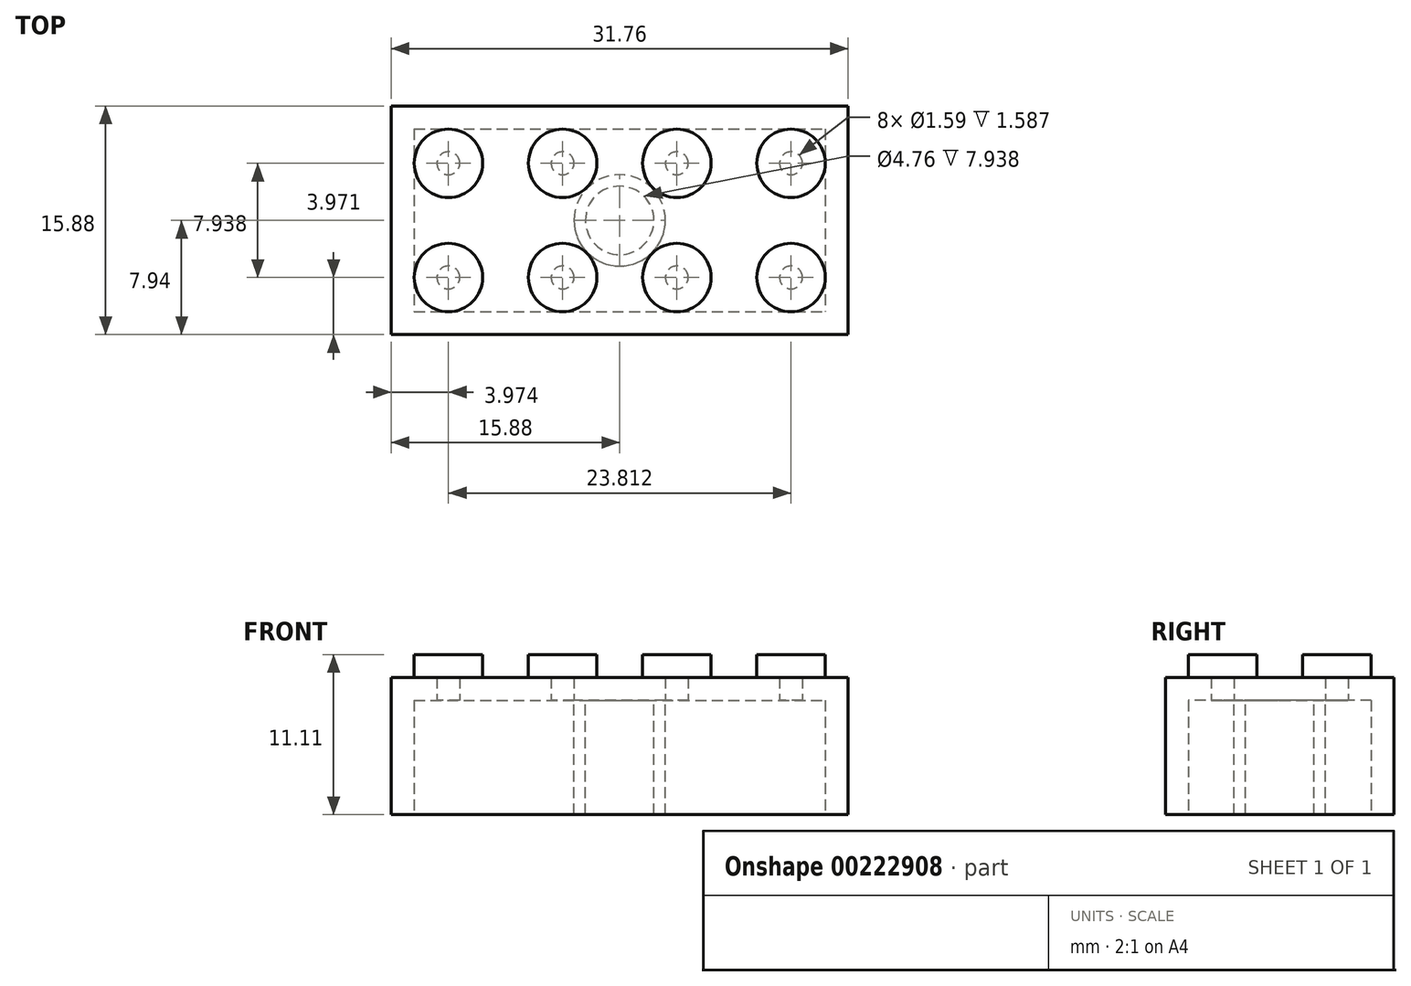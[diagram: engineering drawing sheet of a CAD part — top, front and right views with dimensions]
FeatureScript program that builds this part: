
annotation { "Feature Type Name" : "Feature", "Feature Type Description" : "" }
export const myFeature = defineFeature(function(context is Context, id is Id, definition is map)
    precondition{}
    {
        {
            var Q0;
            Q0=qCreatedBy(makeId("Top.planeOp"),FACE);
            var sketch = newSketch(context, id + "F0", { "sketchPlane" : qUnion([Q0])});
            skLineSegment(sketch, "E0.bottom", {"start": v(-15.88, 7.94) * mm, "end": v(15.88, 7.94) * mm});
            skLineSegment(sketch, "E0.top", {"start": v(-15.88, -7.94) * mm, "end": v(15.88, -7.94) * mm});
            skLineSegment(sketch, "E0.left", {"start": v(-15.88, 7.94) * mm, "end": v(-15.88, -7.94) * mm});
            skLineSegment(sketch, "E0.right", {"start": v(15.88, 7.94) * mm, "end": v(15.88, -7.94) * mm});
            skPoint(sketch, "E0.middle", {"position": v(0, 0) * mm});
            skCircle(sketch, "E1", {"center": v(-11.9, 3.97) * mm, "radius": 2.38 * mm});
            skCircle(sketch, "E2.0.1.0", {"center": v(-11.9, -3.97) * mm, "radius": 2.38 * mm});
            skCircle(sketch, "E2.1.0.0", {"center": v(-3.97, 3.97) * mm, "radius": 2.38 * mm});
            skCircle(sketch, "E2.1.1.0", {"center": v(-3.97, -3.97) * mm, "radius": 2.38 * mm});
            skLineSegment(sketch, "E2.direction1", {"start": v(-11.9, 3.97) * mm, "end": v(-3.97, 3.97) * mm, "construction": true});
            skLineSegment(sketch, "E2.direction2", {"start": v(-11.9, 3.97) * mm, "end": v(-11.9, -3.97) * mm, "construction": true});
            skCircle(sketch, "E3.0.2.0", {"center": v(3.97, 3.97) * mm, "radius": 2.38 * mm});
            skCircle(sketch, "E3.0.2.1", {"center": v(3.97, -3.97) * mm, "radius": 2.38 * mm});
            skCircle(sketch, "E3.0.3.0", {"center": v(11.9, 3.97) * mm, "radius": 2.38 * mm});
            skCircle(sketch, "E3.0.3.1", {"center": v(11.9, -3.97) * mm, "radius": 2.38 * mm});
            skSolve(sketch);
        }
        {
            var Q0;
            Q0=makeQuery(id+"F0.imprint","IMPRINT",FACE,{"disambiguationData":[TD([[makeQuery(id+"F0.imprint","IMPRINT",EDGE,{"derivedFrom":sQuery(id+"F0.wireOp",EDGE,"E0.bottom")}),-1.0]])]});
            extrude(context, id + "F1", {"entities" : qUnion([Q0]), "depth" : 3.17 * mm});
        }
        {
            var Q0;
            Q0=makeQuery(id+"F0.imprint","IMPRINT",FACE,{"disambiguationData":[TD([[makeQuery(id+"F0.imprint","IMPRINT",EDGE,{"derivedFrom":sQuery(id+"F0.wireOp",EDGE,"E1")}),1.0]])]});
            var Q1;
            Q1=makeQuery(id+"F0.imprint","IMPRINT",FACE,{"disambiguationData":[TD([[makeQuery(id+"F0.imprint","IMPRINT",EDGE,{"derivedFrom":sQuery(id+"F0.wireOp",EDGE,"E2.1.0.0")}),1.0]])]});
            var Q2;
            Q2=makeQuery(id+"F0.imprint","IMPRINT",FACE,{"disambiguationData":[TD([[makeQuery(id+"F0.imprint","IMPRINT",EDGE,{"derivedFrom":sQuery(id+"F0.wireOp",EDGE,"E2.1.1.0")}),1.0]])]});
            var Q3;
            Q3=makeQuery(id+"F0.imprint","IMPRINT",FACE,{"disambiguationData":[TD([[makeQuery(id+"F0.imprint","IMPRINT",EDGE,{"derivedFrom":sQuery(id+"F0.wireOp",EDGE,"E2.0.1.0")}),1.0]])]});
            var Q4;
            Q4=makeQuery(id+"F0.imprint","IMPRINT",FACE,{"disambiguationData":[TD([[makeQuery(id+"F0.imprint","IMPRINT",EDGE,{"derivedFrom":sQuery(id+"F0.wireOp",EDGE,"E3.0.2.0")}),1.0]])]});
            var Q5;
            Q5=makeQuery(id+"F0.imprint","IMPRINT",FACE,{"disambiguationData":[TD([[makeQuery(id+"F0.imprint","IMPRINT",EDGE,{"derivedFrom":sQuery(id+"F0.wireOp",EDGE,"E3.0.3.0")}),1.0]])]});
            var Q6;
            Q6=makeQuery(id+"F0.imprint","IMPRINT",FACE,{"disambiguationData":[TD([[makeQuery(id+"F0.imprint","IMPRINT",EDGE,{"derivedFrom":sQuery(id+"F0.wireOp",EDGE,"E3.0.3.1")}),1.0]])]});
            var Q7;
            Q7=makeQuery(id+"F0.imprint","IMPRINT",FACE,{"disambiguationData":[TD([[makeQuery(id+"F0.imprint","IMPRINT",EDGE,{"derivedFrom":sQuery(id+"F0.wireOp",EDGE,"E3.0.2.1")}),1.0]])]});
            extrude(context, id + "F2", {"entities" : qUnion([Q0, Q1, Q2, Q3, Q4, Q5, Q6, Q7]), "operationType" : NewBodyOperationType.ADD, "depth" : 4.76 * mm});
        }
        {
            var Q0;
            {var subQ0=sQuery(id+"F0.wireOp",EDGE,"E2.1.1.0");var subQ1=sQuery(id+"F0.wireOp",EDGE,"E2.1.0.0");var subQ2=sQuery(id+"F0.wireOp",EDGE,"E2.0.1.0");var subQ3=sQuery(id+"F0.wireOp",EDGE,"E1");Q0=makeQuery(id+"F2.boolean.opBoolean","MERGE",FACE,{"derivedFrom":[makeQuery(id+"F1.opExtrude","CAP_FACE",FACE,{"disambiguationData":[OSD([sQuery(id+"F0.wireOp",EDGE,"E0.bottom"),sQuery(id+"F0.wireOp",EDGE,"E0.top"),sQuery(id+"F0.wireOp",EDGE,"E0.left"),sQuery(id+"F0.wireOp",EDGE,"E0.right"),subQ3,subQ2,subQ1,subQ0])],"isStart":true}),makeQuery(id+"F2.opExtrude","CAP_FACE",FACE,{"disambiguationData":[OSD([subQ3])],"isStart":true}),makeQuery(id+"F2.opExtrude","CAP_FACE",FACE,{"disambiguationData":[OSD([subQ2])],"isStart":true}),makeQuery(id+"F2.opExtrude","CAP_FACE",FACE,{"disambiguationData":[OSD([subQ1])],"isStart":true}),makeQuery(id+"F2.opExtrude","CAP_FACE",FACE,{"disambiguationData":[OSD([subQ0])],"isStart":true})]});}
            shell(context, id + "F3", {"entities" : qUnion([Q0]), "thickness" : 1.59 * mm});
        }
        {
            var Q0;
            Q0=makeQuery(id+"F3.opShell","OFFSET_FACE",FACE,{"disambiguationData":[OSD([sQuery(id+"F0.wireOp",EDGE,"E0.bottom"),sQuery(id+"F0.wireOp",EDGE,"E0.top"),sQuery(id+"F0.wireOp",EDGE,"E0.left"),sQuery(id+"F0.wireOp",EDGE,"E0.right"),sQuery(id+"F0.wireOp",EDGE,"E1"),sQuery(id+"F0.wireOp",EDGE,"E2.0.1.0"),sQuery(id+"F0.wireOp",EDGE,"E2.1.0.0"),sQuery(id+"F0.wireOp",EDGE,"E2.1.1.0")])]});
            var sketch = newSketch(context, id + "F4", { "sketchPlane" : qUnion([Q0])});
            skCircle(sketch, "E4", {"center": v(0, 0) * mm, "radius": 3.18 * mm});
            skCircle(sketch, "E5", {"center": v(0, 0) * mm, "radius": 2.38 * mm});
            skSolve(sketch);
        }
        {
            var Q0;
            Q0=makeQuery(id+"F4.imprint","IMPRINT",FACE,{"disambiguationData":[TD([[makeQuery(id+"F4.imprint","IMPRINT",EDGE,{"derivedFrom":sQuery(id+"F4.wireOp",EDGE,"E4")}),1.0]])]});
            extrude(context, id + "F5", {"entities" : qUnion([Q0]), "operationType" : NewBodyOperationType.ADD, "depth" : 1.59 * mm});
        }
        {
            var Q0;
            {var subQ0=sQuery(id+"F0.wireOp",EDGE,"E3.0.3.1");var subQ1=sQuery(id+"F0.wireOp",EDGE,"E3.0.3.0");var subQ2=sQuery(id+"F0.wireOp",EDGE,"E3.0.2.1");var subQ3=sQuery(id+"F0.wireOp",EDGE,"E3.0.2.0");var subQ4=sQuery(id+"F0.wireOp",EDGE,"E2.1.1.0");var subQ5=sQuery(id+"F0.wireOp",EDGE,"E2.1.0.0");var subQ6=sQuery(id+"F0.wireOp",EDGE,"E2.0.1.0");var subQ7=sQuery(id+"F0.wireOp",EDGE,"E1");Q0=makeQuery(id+"F2.boolean.opBoolean","MERGE",FACE,{"derivedFrom":[makeQuery(id+"F1.opExtrude","CAP_FACE",FACE,{"disambiguationData":[OSD([sQuery(id+"F0.wireOp",EDGE,"E0.bottom"),sQuery(id+"F0.wireOp",EDGE,"E0.top"),sQuery(id+"F0.wireOp",EDGE,"E0.left"),sQuery(id+"F0.wireOp",EDGE,"E0.right"),subQ7,subQ6,subQ5,subQ4,subQ3,subQ2,subQ1,subQ0])],"isStart":true}),makeQuery(id+"F2.opExtrude","CAP_FACE",FACE,{"disambiguationData":[OSD([subQ7])],"isStart":true}),makeQuery(id+"F2.opExtrude","CAP_FACE",FACE,{"disambiguationData":[OSD([subQ6])],"isStart":true}),makeQuery(id+"F2.opExtrude","CAP_FACE",FACE,{"disambiguationData":[OSD([subQ5])],"isStart":true}),makeQuery(id+"F2.opExtrude","CAP_FACE",FACE,{"disambiguationData":[OSD([subQ4])],"isStart":true}),makeQuery(id+"F2.opExtrude","CAP_FACE",FACE,{"disambiguationData":[OSD([subQ3])],"isStart":true}),makeQuery(id+"F2.opExtrude","CAP_FACE",FACE,{"disambiguationData":[OSD([subQ2])],"isStart":true}),makeQuery(id+"F2.opExtrude","CAP_FACE",FACE,{"disambiguationData":[OSD([subQ1])],"isStart":true}),makeQuery(id+"F2.opExtrude","CAP_FACE",FACE,{"disambiguationData":[OSD([subQ0])],"isStart":true})]});}
            var Q1;
            Q1=makeQuery(id+"F5.opExtrude","CAP_FACE",FACE,{"disambiguationData":[OSD([sQuery(id+"F4.wireOp",EDGE,"E4"),sQuery(id+"F4.wireOp",EDGE,"E5")])],"isStart":false});
            extrude(context, id + "F6", {"entities" : qUnion([Q0, Q1]), "operationType" : NewBodyOperationType.ADD, "depth" : 6.35 * mm});
        }
    });
